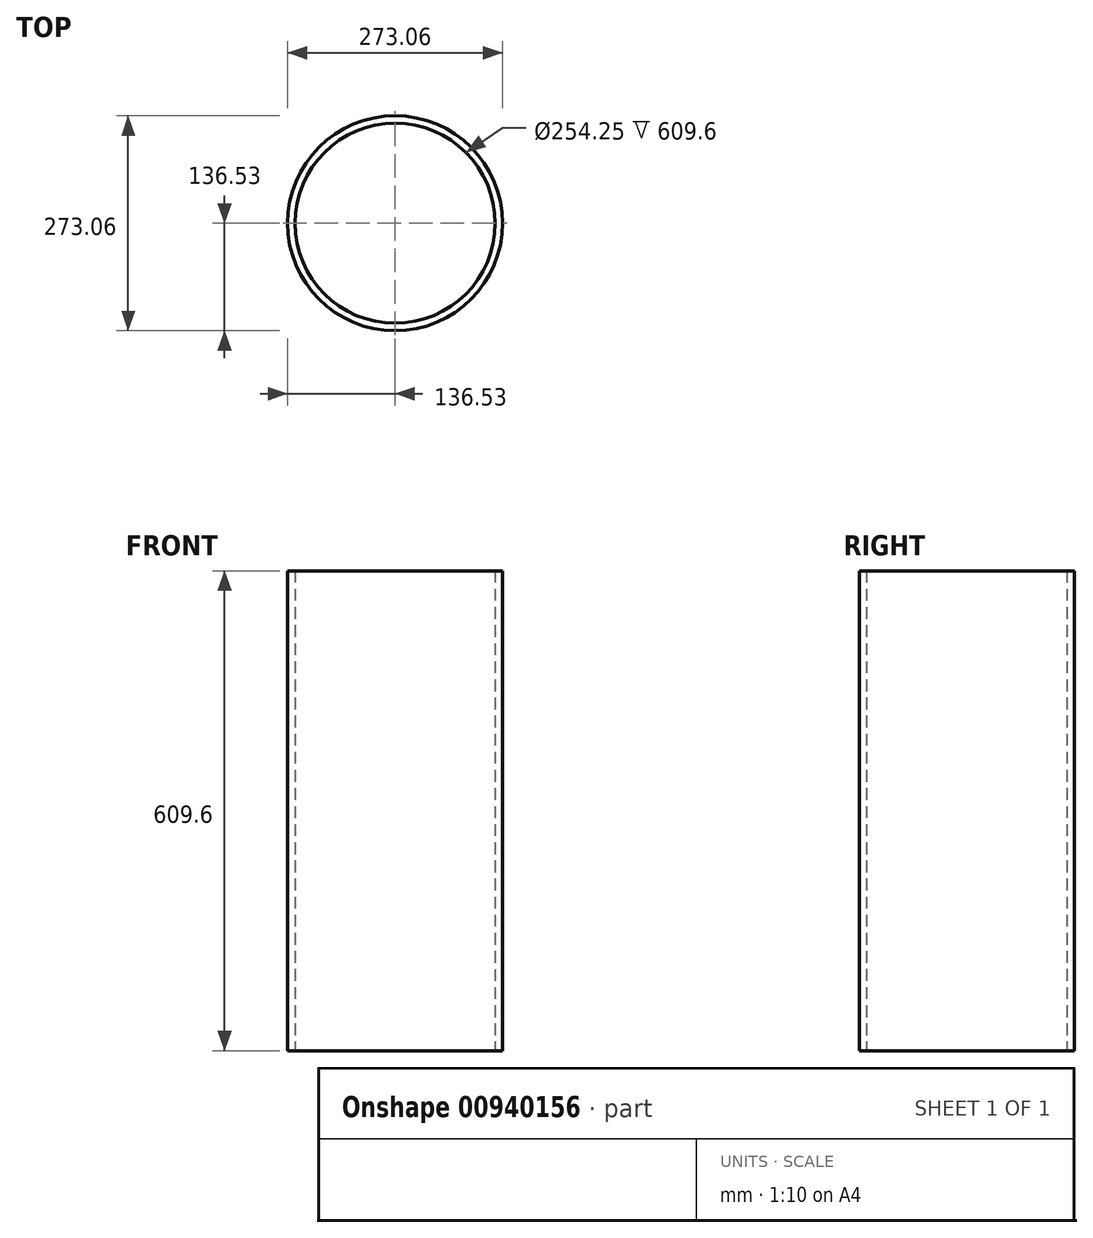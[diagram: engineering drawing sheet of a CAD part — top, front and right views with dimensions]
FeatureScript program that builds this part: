
annotation { "Feature Type Name" : "Feature", "Feature Type Description" : "" }
export const myFeature = defineFeature(function(context is Context, id is Id, definition is map)
    precondition{}
    {
        {
            var Q0;
            Q0=qCreatedBy(makeId("Top.planeOp"),FACE);
            var sketch = newSketch(context, id + "F0", { "sketchPlane" : qUnion([Q0])});
            skCircle(sketch, "E0", {"center": v(0, 0) * mm, "radius": 127.13 * mm});
            skCircle(sketch, "E1", {"center": v(0, 0) * mm, "radius": 136.53 * mm});
            skSolve(sketch);
        }
        {
            var Q0;
            Q0=qSketchRegion(id+"F0",true);
            extrude(context, id + "F1", {"entities" : qUnion([Q0]), "depth" : 609.6 * mm, "offsetDistance" : 25.4 * mm});
        }
        {
            var Q0;
            Q0=qCreatedBy(makeId("Front.planeOp"),FACE);
            cPlane(context, id + "F2", {"entities" : qUnion([Q0]), "cplaneType" : CPlaneType.OFFSET, "offset" : 0 * mm, "width" : 152.4 * mm, "height" : 152.4 * mm});
        }
    });
